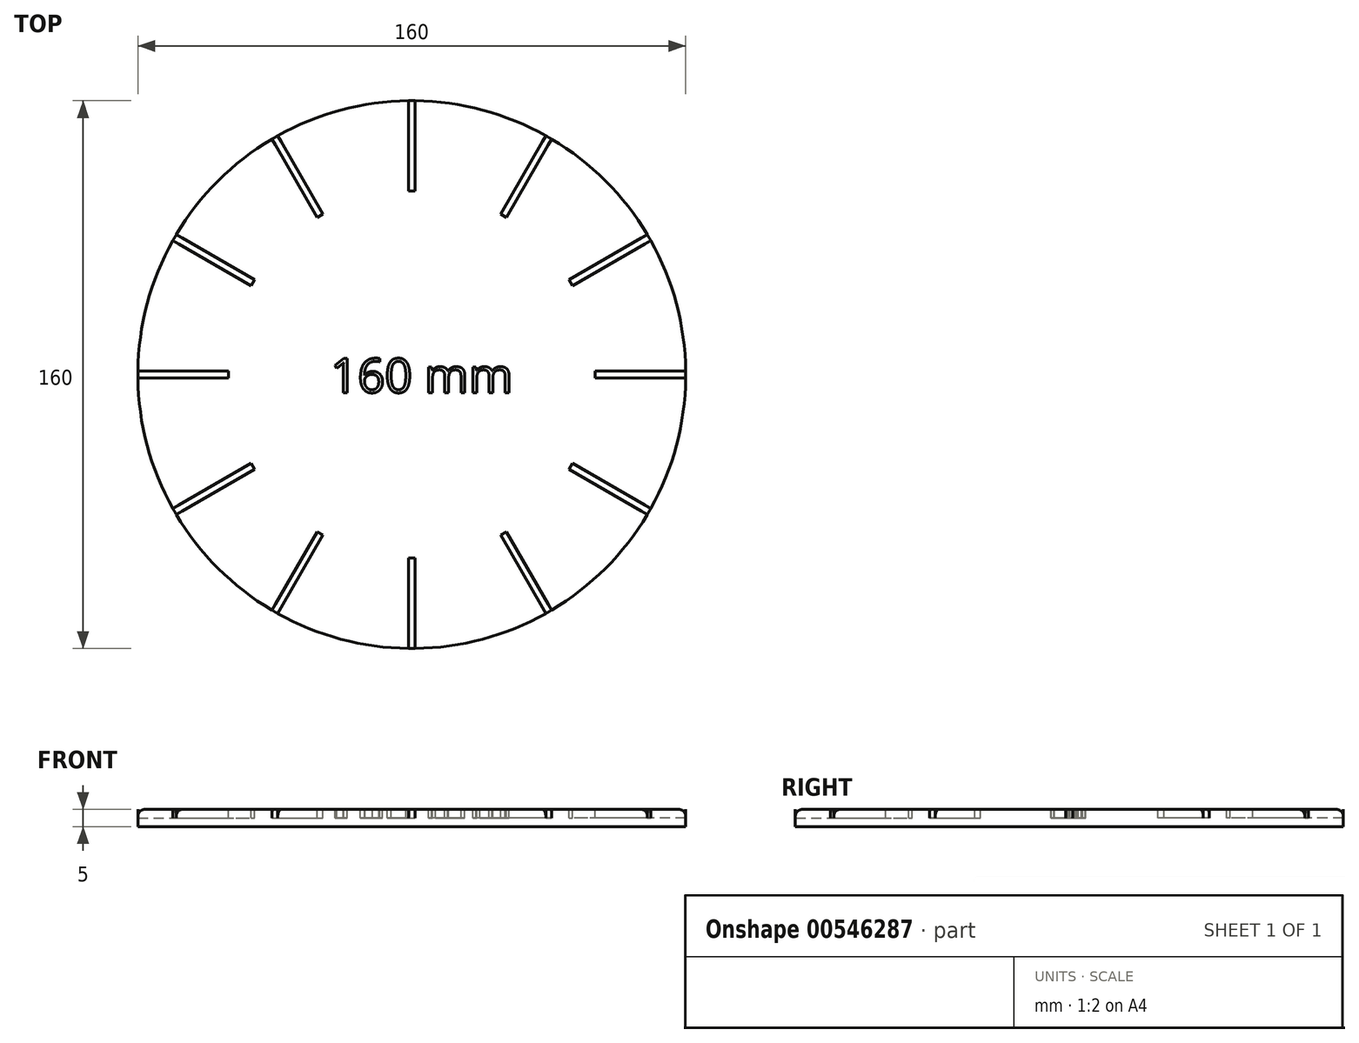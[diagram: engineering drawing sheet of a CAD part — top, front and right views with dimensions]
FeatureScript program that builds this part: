
annotation { "Feature Type Name" : "Feature", "Feature Type Description" : "" }
export const myFeature = defineFeature(function(context is Context, id is Id, definition is map)
    precondition{}
    {
        {
            var Q0;
            Q0=qCreatedBy(makeId("Top.planeOp"),FACE);
            var sketch = newSketch(context, id + "F0", { "sketchPlane" : qUnion([Q0])});
            skCircle(sketch, "E0", {"center": v(0, 0) * mm, "radius": 80 * mm});
            skSolve(sketch);
        }
        {
            var Q0;
            Q0=qSketchRegion(id+"F0",true);
            extrude(context, id + "F1", {"entities" : qUnion([Q0]), "depth" : 5 * mm, "offsetDistance" : 25 * mm});
        }
        {
            var Q0;
            Q0=makeQuery(id+"F1.opExtrude","CAP_FACE",FACE,{"disambiguationData":[OSD([sQuery(id+"F0.wireOp",EDGE,"E0")])],"isStart":false});
            var sketch = newSketch(context, id + "F2", { "sketchPlane" : qUnion([Q0])});
            skLineSegment(sketch, "E1.bottom", {"start": v(-1, 80) * mm, "end": v(1, 80) * mm});
            skLineSegment(sketch, "E1.top", {"start": v(-1, 53.58) * mm, "end": v(1, 53.58) * mm});
            skLineSegment(sketch, "E1.left", {"start": v(-1, 80) * mm, "end": v(-1, 53.58) * mm});
            skLineSegment(sketch, "E1.right", {"start": v(1, 80) * mm, "end": v(1, 53.58) * mm});
            skLineSegment(sketch, "E2.1.0", {"start": v(-40.86, 68.78) * mm, "end": v(-27.65, 45.9) * mm});
            skLineSegment(sketch, "E2.1.1", {"start": v(-39.13, 69.78) * mm, "end": v(-25.92, 46.9) * mm});
            skLineSegment(sketch, "E2.1.2", {"start": v(-27.65, 45.9) * mm, "end": v(-25.92, 46.9) * mm});
            skLineSegment(sketch, "E2.1.3", {"start": v(-40.86, 68.78) * mm, "end": v(-39.13, 69.78) * mm});
            skLineSegment(sketch, "E2.2.0", {"start": v(-69.78, 39.13) * mm, "end": v(-46.9, 25.92) * mm});
            skLineSegment(sketch, "E2.2.1", {"start": v(-68.78, 40.86) * mm, "end": v(-45.9, 27.65) * mm});
            skLineSegment(sketch, "E2.2.2", {"start": v(-46.9, 25.92) * mm, "end": v(-45.9, 27.65) * mm});
            skLineSegment(sketch, "E2.2.3", {"start": v(-69.78, 39.13) * mm, "end": v(-68.78, 40.86) * mm});
            skPoint(sketch, "E2.center", {"position": v(0, 0) * mm});
            skLineSegment(sketch, "E3.2.3.0", {"start": v(-80, -1) * mm, "end": v(-53.58, -1) * mm});
            skLineSegment(sketch, "E3.3.3.0", {"start": v(-80, 1) * mm, "end": v(-53.58, 1) * mm});
            skLineSegment(sketch, "E3.6.3.0", {"start": v(-53.58, -1) * mm, "end": v(-53.58, 1) * mm});
            skLineSegment(sketch, "E3.9.3.0", {"start": v(-80, -1) * mm, "end": v(-80, 1) * mm});
            skLineSegment(sketch, "E3.2.4.0", {"start": v(-68.78, -40.86) * mm, "end": v(-45.9, -27.65) * mm});
            skLineSegment(sketch, "E3.3.4.0", {"start": v(-69.78, -39.13) * mm, "end": v(-46.9, -25.92) * mm});
            skLineSegment(sketch, "E3.6.4.0", {"start": v(-45.9, -27.65) * mm, "end": v(-46.9, -25.92) * mm});
            skLineSegment(sketch, "E3.9.4.0", {"start": v(-68.78, -40.86) * mm, "end": v(-69.78, -39.13) * mm});
            skLineSegment(sketch, "E3.2.5.0", {"start": v(-39.13, -69.78) * mm, "end": v(-25.92, -46.9) * mm});
            skLineSegment(sketch, "E3.3.5.0", {"start": v(-40.86, -68.78) * mm, "end": v(-27.65, -45.9) * mm});
            skLineSegment(sketch, "E3.6.5.0", {"start": v(-25.92, -46.9) * mm, "end": v(-27.65, -45.9) * mm});
            skLineSegment(sketch, "E3.9.5.0", {"start": v(-39.13, -69.78) * mm, "end": v(-40.86, -68.78) * mm});
            skLineSegment(sketch, "E3.2.6.0", {"start": v(1, -80) * mm, "end": v(1, -53.58) * mm});
            skLineSegment(sketch, "E3.3.6.0", {"start": v(-1, -80) * mm, "end": v(-1, -53.58) * mm});
            skLineSegment(sketch, "E3.6.6.0", {"start": v(1, -53.58) * mm, "end": v(-1, -53.58) * mm});
            skLineSegment(sketch, "E3.9.6.0", {"start": v(1, -80) * mm, "end": v(-1, -80) * mm});
            skLineSegment(sketch, "E3.2.7.0", {"start": v(40.86, -68.78) * mm, "end": v(27.65, -45.9) * mm});
            skLineSegment(sketch, "E3.3.7.0", {"start": v(39.13, -69.78) * mm, "end": v(25.92, -46.9) * mm});
            skLineSegment(sketch, "E3.6.7.0", {"start": v(27.65, -45.9) * mm, "end": v(25.92, -46.9) * mm});
            skLineSegment(sketch, "E3.9.7.0", {"start": v(40.86, -68.78) * mm, "end": v(39.13, -69.78) * mm});
            skLineSegment(sketch, "E3.2.8.0", {"start": v(69.78, -39.13) * mm, "end": v(46.9, -25.92) * mm});
            skLineSegment(sketch, "E3.3.8.0", {"start": v(68.78, -40.86) * mm, "end": v(45.9, -27.65) * mm});
            skLineSegment(sketch, "E3.6.8.0", {"start": v(46.9, -25.92) * mm, "end": v(45.9, -27.65) * mm});
            skLineSegment(sketch, "E3.9.8.0", {"start": v(69.78, -39.13) * mm, "end": v(68.78, -40.86) * mm});
            skLineSegment(sketch, "E3.2.9.0", {"start": v(80, 1) * mm, "end": v(53.58, 1) * mm});
            skLineSegment(sketch, "E3.3.9.0", {"start": v(80, -1) * mm, "end": v(53.58, -1) * mm});
            skLineSegment(sketch, "E3.6.9.0", {"start": v(53.58, 1) * mm, "end": v(53.58, -1) * mm});
            skLineSegment(sketch, "E3.9.9.0", {"start": v(80, 1) * mm, "end": v(80, -1) * mm});
            skLineSegment(sketch, "E3.2.10.0", {"start": v(68.78, 40.86) * mm, "end": v(45.9, 27.65) * mm});
            skLineSegment(sketch, "E3.3.10.0", {"start": v(69.78, 39.13) * mm, "end": v(46.9, 25.92) * mm});
            skLineSegment(sketch, "E3.6.10.0", {"start": v(45.9, 27.65) * mm, "end": v(46.9, 25.92) * mm});
            skLineSegment(sketch, "E3.9.10.0", {"start": v(68.78, 40.86) * mm, "end": v(69.78, 39.13) * mm});
            skLineSegment(sketch, "E3.2.11.0", {"start": v(39.13, 69.78) * mm, "end": v(25.92, 46.9) * mm});
            skLineSegment(sketch, "E3.3.11.0", {"start": v(40.86, 68.78) * mm, "end": v(27.65, 45.9) * mm});
            skLineSegment(sketch, "E3.6.11.0", {"start": v(25.92, 46.9) * mm, "end": v(27.65, 45.9) * mm});
            skLineSegment(sketch, "E3.9.11.0", {"start": v(39.13, 69.78) * mm, "end": v(40.86, 68.78) * mm});
            skSolve(sketch);
        }
        {
            var Q0;
            Q0=qSketchRegion(id+"F2",true);
            extrude(context, id + "F3", {"entities" : qUnion([Q0]), "operationType" : NewBodyOperationType.REMOVE, "oppositeDirection" : true, "depth" : 2.5 * mm, "offsetDistance" : 25 * mm});
        }
        {
            var Q0;
            Q0=makeQuery(id+"F1.opExtrude","CAP_FACE",FACE,{"disambiguationData":[OSD([sQuery(id+"F0.wireOp",EDGE,"E0")])],"isStart":false});
            var sketch = newSketch(context, id + "F4", { "sketchPlane" : qUnion([Q0])});
            skText(sketch, "E4", { "text": "160 mm\n", "fontName": "OpenSans-Regular.ttf"});
            const initialGuessF4  = {"E4": [-0.02373, -0.00525, 1, 0, 0.01]};
            skSetInitialGuess(sketch, initialGuessF4);
            skSolve(sketch);
        }
        {
            var Q0;
            Q0=qSketchRegion(id+"F4",true);
            extrude(context, id + "F5", {"entities" : qUnion([Q0]), "operationType" : NewBodyOperationType.REMOVE, "oppositeDirection" : true, "depth" : 2.5 * mm, "offsetDistance" : 25 * mm});
        }
        {
            var Q0;
            {var subQ0=sQuery(id+"F0.wireOp",EDGE,"E0");Q0=makeQuery(id+"F3.boolean.opBoolean","SPLIT",EDGE,{"disambiguationData":[TD([makeQuery(id+"F3.opExtrude","SWEPT_FACE",FACE,{"disambiguationData":[OSD([sQuery(id+"F2.wireOp",EDGE,"E3.2.6.0")])]})])],"derivedFrom":makeQuery(id+"F1.opExtrude","CAP_EDGE",EDGE,{"disambiguationData":[OSD([subQ0])],"isStart":false})});}
            var Q1;
            {var subQ0=sQuery(id+"F0.wireOp",EDGE,"E0");Q1=makeQuery(id+"F3.boolean.opBoolean","SPLIT",EDGE,{"disambiguationData":[TD([makeQuery(id+"F3.opExtrude","SWEPT_FACE",FACE,{"disambiguationData":[OSD([sQuery(id+"F2.wireOp",EDGE,"E3.2.5.0")])]})])],"derivedFrom":makeQuery(id+"F1.opExtrude","CAP_EDGE",EDGE,{"disambiguationData":[OSD([subQ0])],"isStart":false})});}
            var Q2;
            {var subQ0=sQuery(id+"F0.wireOp",EDGE,"E0");Q2=makeQuery(id+"F3.boolean.opBoolean","SPLIT",EDGE,{"disambiguationData":[TD([makeQuery(id+"F3.opExtrude","SWEPT_FACE",FACE,{"disambiguationData":[OSD([sQuery(id+"F2.wireOp",EDGE,"E3.2.4.0")])]})])],"derivedFrom":makeQuery(id+"F1.opExtrude","CAP_EDGE",EDGE,{"disambiguationData":[OSD([subQ0])],"isStart":false})});}
            var Q3;
            {var subQ0=sQuery(id+"F0.wireOp",EDGE,"E0");Q3=makeQuery(id+"F3.boolean.opBoolean","SPLIT",EDGE,{"disambiguationData":[TD([makeQuery(id+"F3.opExtrude","SWEPT_FACE",FACE,{"disambiguationData":[OSD([sQuery(id+"F2.wireOp",EDGE,"E3.2.3.0")])]})])],"derivedFrom":makeQuery(id+"F1.opExtrude","CAP_EDGE",EDGE,{"disambiguationData":[OSD([subQ0])],"isStart":false})});}
            var Q4;
            {var subQ0=sQuery(id+"F0.wireOp",EDGE,"E0");Q4=makeQuery(id+"F3.boolean.opBoolean","SPLIT",EDGE,{"disambiguationData":[TD([makeQuery(id+"F3.opExtrude","SWEPT_FACE",FACE,{"disambiguationData":[OSD([sQuery(id+"F2.wireOp",EDGE,"E2.2.0")])]})])],"derivedFrom":makeQuery(id+"F1.opExtrude","CAP_EDGE",EDGE,{"disambiguationData":[OSD([subQ0])],"isStart":false})});}
            var Q5;
            {var subQ0=sQuery(id+"F0.wireOp",EDGE,"E0");Q5=makeQuery(id+"F3.boolean.opBoolean","SPLIT",EDGE,{"disambiguationData":[TD([makeQuery(id+"F3.opExtrude","SWEPT_FACE",FACE,{"disambiguationData":[OSD([sQuery(id+"F2.wireOp",EDGE,"E3.2.7.0")])]})])],"derivedFrom":makeQuery(id+"F1.opExtrude","CAP_EDGE",EDGE,{"disambiguationData":[OSD([subQ0])],"isStart":false})});}
            var Q6;
            {var subQ0=sQuery(id+"F0.wireOp",EDGE,"E0");Q6=makeQuery(id+"F3.boolean.opBoolean","SPLIT",EDGE,{"disambiguationData":[TD([makeQuery(id+"F3.opExtrude","SWEPT_FACE",FACE,{"disambiguationData":[OSD([sQuery(id+"F2.wireOp",EDGE,"E3.2.8.0")])]})])],"derivedFrom":makeQuery(id+"F1.opExtrude","CAP_EDGE",EDGE,{"disambiguationData":[OSD([subQ0])],"isStart":false})});}
            var Q7;
            {var subQ0=sQuery(id+"F0.wireOp",EDGE,"E0");Q7=makeQuery(id+"F3.boolean.opBoolean","SPLIT",EDGE,{"disambiguationData":[TD([makeQuery(id+"F3.opExtrude","SWEPT_FACE",FACE,{"disambiguationData":[OSD([sQuery(id+"F2.wireOp",EDGE,"E3.2.9.0")])]})])],"derivedFrom":makeQuery(id+"F1.opExtrude","CAP_EDGE",EDGE,{"disambiguationData":[OSD([subQ0])],"isStart":false})});}
            var Q8;
            {var subQ0=sQuery(id+"F0.wireOp",EDGE,"E0");Q8=makeQuery(id+"F3.boolean.opBoolean","SPLIT",EDGE,{"disambiguationData":[TD([makeQuery(id+"F3.opExtrude","SWEPT_FACE",FACE,{"disambiguationData":[OSD([sQuery(id+"F2.wireOp",EDGE,"E3.2.10.0")])]})])],"derivedFrom":makeQuery(id+"F1.opExtrude","CAP_EDGE",EDGE,{"disambiguationData":[OSD([subQ0])],"isStart":false})});}
            var Q9;
            {var subQ0=sQuery(id+"F0.wireOp",EDGE,"E0");Q9=makeQuery(id+"F3.boolean.opBoolean","SPLIT",EDGE,{"disambiguationData":[TD([makeQuery(id+"F3.opExtrude","SWEPT_FACE",FACE,{"disambiguationData":[OSD([sQuery(id+"F2.wireOp",EDGE,"E1.right")])]})])],"derivedFrom":makeQuery(id+"F1.opExtrude","CAP_EDGE",EDGE,{"disambiguationData":[OSD([subQ0])],"isStart":false})});}
            var Q10;
            {var subQ0=sQuery(id+"F0.wireOp",EDGE,"E0");Q10=makeQuery(id+"F3.boolean.opBoolean","SPLIT",EDGE,{"disambiguationData":[TD([makeQuery(id+"F3.opExtrude","SWEPT_FACE",FACE,{"disambiguationData":[OSD([sQuery(id+"F2.wireOp",EDGE,"E1.left")])]})])],"derivedFrom":makeQuery(id+"F1.opExtrude","CAP_EDGE",EDGE,{"disambiguationData":[OSD([subQ0])],"isStart":false})});}
            var Q11;
            {var subQ0=sQuery(id+"F0.wireOp",EDGE,"E0");Q11=makeQuery(id+"F3.boolean.opBoolean","SPLIT",EDGE,{"disambiguationData":[TD([makeQuery(id+"F3.opExtrude","SWEPT_FACE",FACE,{"disambiguationData":[OSD([sQuery(id+"F2.wireOp",EDGE,"E2.1.0")])]})])],"derivedFrom":makeQuery(id+"F1.opExtrude","CAP_EDGE",EDGE,{"disambiguationData":[OSD([subQ0])],"isStart":false})});}
            fillet(context, id + "F6", {"entities" : qUnion([Q0, Q1, Q2, Q3, Q4, Q5, Q6, Q7, Q8, Q9, Q10, Q11]), "radius" : 2 * mm, "tangentPropagation" : true, "allowEdgeOverflow" : false});
        }
    });
